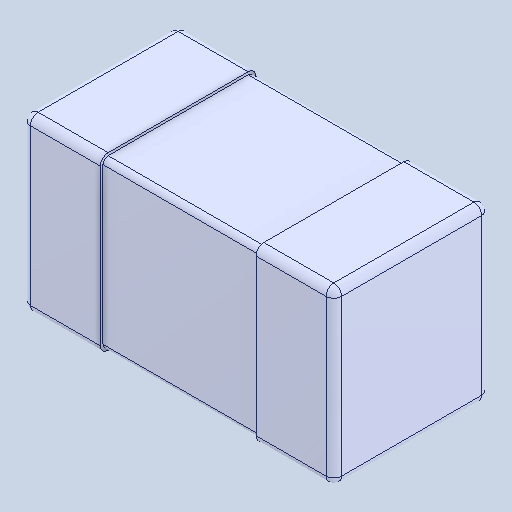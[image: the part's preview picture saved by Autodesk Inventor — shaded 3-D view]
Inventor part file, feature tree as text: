
AUTODESK INVENTOR PART (.ipt)
format: ipt  version: 2025 (Build 290162000, 162)  size: 131,584 bytes
history: native  units: mm
features: fillet x1, mirror x1, other x1
ambient origin geometry x8: Origin, YZ Plane, XZ Plane, XY Plane, X Axis, Y Axis, Z Axis, Center Point
bodies: Solid1 (feature_tree), Solid2 (feature_tree), Solid3 (feature_tree)
feature tree (3):
  fillet  "Fillet1"  [1 undecoded]
  mirror  "Mirror2"
  other  "Boss-Extrude2"
note: 1 required parameter value undecoded (feature->parameter linkage not recoverable at this tier; creation-order binding heuristic only, values carry confidence <= 0.55)
